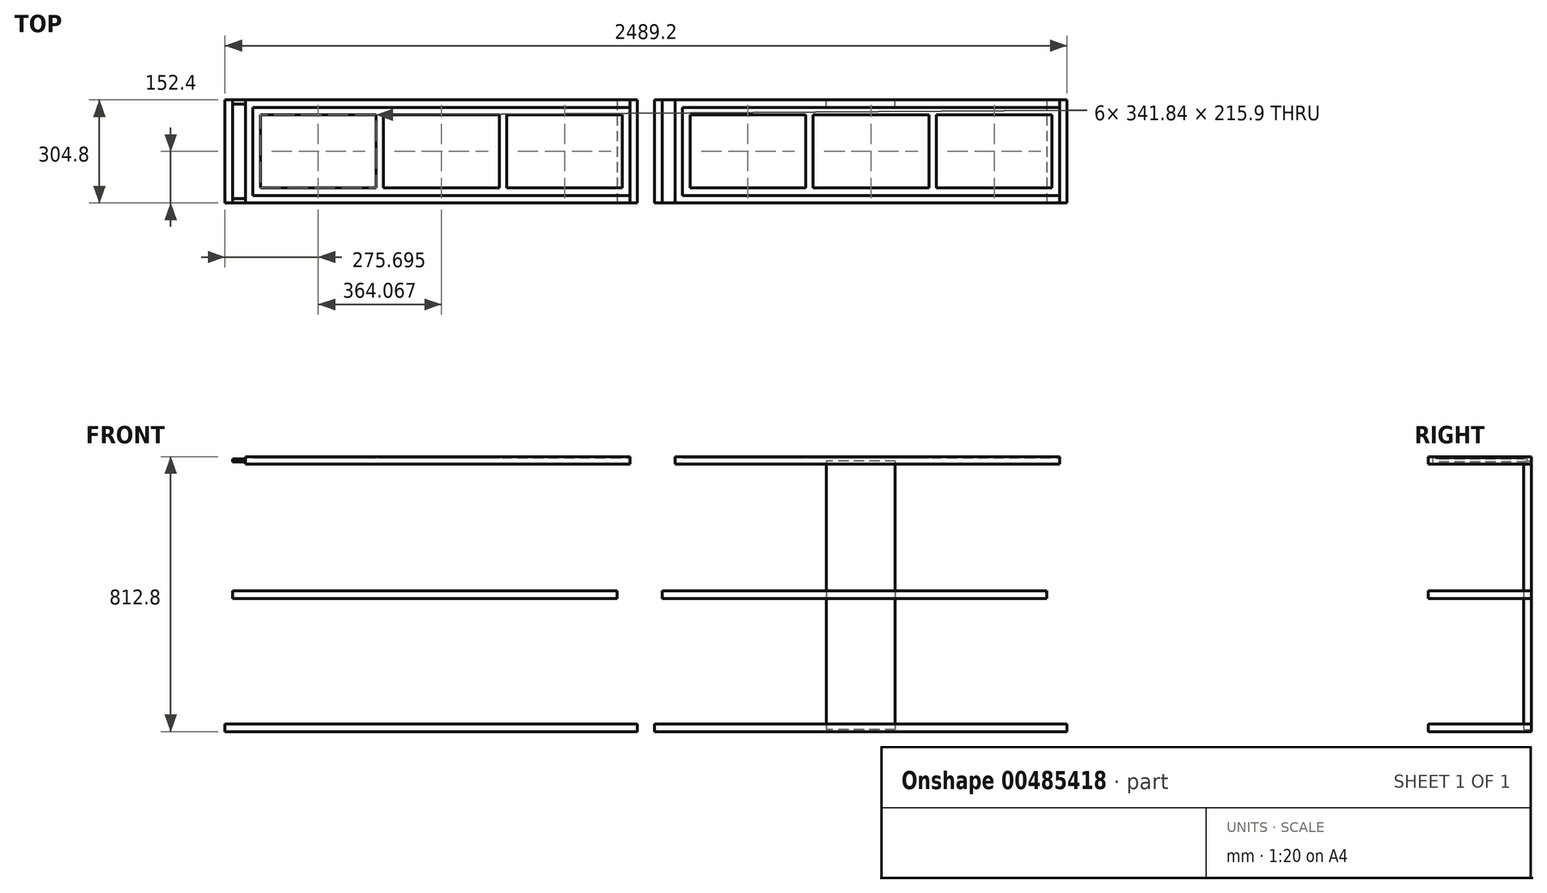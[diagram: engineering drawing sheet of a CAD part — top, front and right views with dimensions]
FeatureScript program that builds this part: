
annotation { "Feature Type Name" : "Feature", "Feature Type Description" : "" }
export const myFeature = defineFeature(function(context is Context, id is Id, definition is map)
    precondition{}
    {
        {
            var Q0;
            Q0=qCreatedBy(makeId("Front.planeOp"),FACE);
            var sketch = newSketch(context, id + "F0", { "sketchPlane" : qUnion([Q0])});
            skLineSegment(sketch, "E0.bottom", {"start": v(0, 22.22) * mm, "end": v(-1219.2, 22.22) * mm});
            skLineSegment(sketch, "E0.top", {"start": v(0, 0) * mm, "end": v(-1219.2, 0) * mm});
            skLineSegment(sketch, "E0.left", {"start": v(0, 22.22) * mm, "end": v(0, 0) * mm});
            skLineSegment(sketch, "E0.right", {"start": v(-1219.2, 22.22) * mm, "end": v(-1219.2, 0) * mm});
            skLineSegment(sketch, "E1.bottom", {"start": v(0, 22.22) * mm, "end": v(-22.23, 22.22) * mm});
            skLineSegment(sketch, "E1.top", {"start": v(0, 812.8) * mm, "end": v(-22.23, 812.8) * mm});
            skLineSegment(sketch, "E1.left", {"start": v(0, 22.22) * mm, "end": v(0, 812.8) * mm});
            skLineSegment(sketch, "E1.right", {"start": v(-22.23, 22.22) * mm, "end": v(-22.23, 812.8) * mm});
            skLineSegment(sketch, "E2.bottom", {"start": v(-1219.2, 22.22) * mm, "end": v(-1196.98, 22.22) * mm});
            skLineSegment(sketch, "E2.top", {"start": v(-1219.2, 812.8) * mm, "end": v(-1196.98, 812.8) * mm});
            skLineSegment(sketch, "E2.left", {"start": v(-1219.2, 22.22) * mm, "end": v(-1219.2, 812.8) * mm});
            skLineSegment(sketch, "E2.right", {"start": v(-1196.98, 22.22) * mm, "end": v(-1196.98, 812.8) * mm});
            skLineSegment(sketch, "E3.bottom", {"start": v(-1196.98, 393.7) * mm, "end": v(-60.33, 393.7) * mm});
            skLineSegment(sketch, "E3.top", {"start": v(-1196.98, 415.93) * mm, "end": v(-60.33, 415.93) * mm});
            skLineSegment(sketch, "E3.left", {"start": v(-1196.98, 393.7) * mm, "end": v(-1196.98, 415.93) * mm});
            skLineSegment(sketch, "E3.right", {"start": v(-60.33, 393.7) * mm, "end": v(-60.33, 415.93) * mm});
            skLineSegment(sketch, "E4.bottom", {"start": v(-22.23, 812.8) * mm, "end": v(-1158.88, 812.8) * mm});
            skLineSegment(sketch, "E4.top", {"start": v(-22.23, 790.58) * mm, "end": v(-1158.88, 790.57) * mm});
            skLineSegment(sketch, "E4.left", {"start": v(-22.23, 812.8) * mm, "end": v(-22.23, 790.58) * mm});
            skLineSegment(sketch, "E5.left", {"start": v(-1158.88, 812.8) * mm, "end": v(-1158.88, 790.57) * mm});
            skSolve(sketch);
        }
        {
            var Q0;
            {var subQ1=sQuery(id+"F0.wireOp",EDGE,"E2.bottom");Q0=makeQuery(id+"F0.imprint","IMPRINT",FACE,{"disambiguationData":[TD([[makeQuery(id+"F0.imprint","IMPRINT",EDGE,{"derivedFrom":subQ1}),1.0]])]});}
            var Q1;
            Q1=makeQuery(id+"F0.imprint","IMPRINT",FACE,{"disambiguationData":[TD([[makeQuery(id+"F0.imprint","IMPRINT",EDGE,{"derivedFrom":sQuery(id+"F0.wireOp",EDGE,"E3.bottom")}),1.0]])]});
            var Q2;
            Q2=makeQuery(id+"F0.imprint","IMPRINT",FACE,{"disambiguationData":[TD([[makeQuery(id+"F0.imprint","IMPRINT",EDGE,{"derivedFrom":sQuery(id+"F0.wireOp",EDGE,"E4.bottom")}),1.0]])]});
            var Q3;
            Q3=makeQuery(id+"F0.imprint","IMPRINT",FACE,{"disambiguationData":[TD([[makeQuery(id+"F0.imprint","IMPRINT",EDGE,{"derivedFrom":sQuery(id+"F0.wireOp",EDGE,"E1.bottom")}),-1.0]])]});
            var Q4;
            Q4=makeQuery(id+"F0.imprint","IMPRINT",FACE,{"disambiguationData":[TD([[makeQuery(id+"F0.imprint","IMPRINT",EDGE,{"derivedFrom":sQuery(id+"F0.wireOp",EDGE,"E0.bottom")}),1.0]])]});
            extrude(context, id + "F1", {"entities" : qUnion([Q0, Q1, Q2, Q3, Q4]), "oppositeDirection" : true, "depth" : 304.8 * mm});
        }
        {
            var Q0;
            Q0=makeQuery(id+"F1.opExtrude","SWEPT_FACE",FACE,{"disambiguationData":[OSD([sQuery(id+"F0.wireOp",EDGE,"E1.top"),sQuery(id+"F0.wireOp",EDGE,"E4.bottom")])]});
            var sketch = newSketch(context, id + "F2", { "sketchPlane" : qUnion([Q0])});
            skLineSegment(sketch, "E6.0", {"start": v(-1136.65, 22.23) * mm, "end": v(-22.23, 22.23) * mm});
            skLineSegment(sketch, "E6.1", {"start": v(-1136.65, 282.58) * mm, "end": v(-1136.65, 22.22) * mm});
            skLineSegment(sketch, "E6.2", {"start": v(-22.23, 282.58) * mm, "end": v(-1136.65, 282.58) * mm});
            skLineSegment(sketch, "E6.3", {"start": v(-22.23, 22.22) * mm, "end": v(-22.23, 282.58) * mm});
            skLineSegment(sketch, "E7.0", {"start": v(-44.45, 260.35) * mm, "end": v(-386.3, 260.35) * mm});
            skLineSegment(sketch, "E7.1", {"start": v(-44.45, 44.45) * mm, "end": v(-44.45, 260.35) * mm});
            skLineSegment(sketch, "E7.2", {"start": v(-1114.43, 44.45) * mm, "end": v(-772.58, 44.45) * mm});
            skLineSegment(sketch, "E7.3", {"start": v(-1114.43, 260.35) * mm, "end": v(-1114.43, 44.45) * mm});
            skLineSegment(sketch, "E8", {"start": v(-772.58, 260.35) * mm, "end": v(-772.58, 44.45) * mm});
            skLineSegment(sketch, "E9", {"start": v(-750.36, 260.35) * mm, "end": v(-750.36, 44.45) * mm});
            skLineSegment(sketch, "E10", {"start": v(-408.52, 260.35) * mm, "end": v(-408.52, 44.45) * mm});
            skLineSegment(sketch, "E11", {"start": v(-386.3, 260.35) * mm, "end": v(-386.3, 44.45) * mm});
            skLineSegment(sketch, "E12.trimOffspring", {"start": v(-772.58, 260.35) * mm, "end": v(-1114.43, 260.35) * mm});
            skLineSegment(sketch, "E13.trimOffspring", {"start": v(-750.36, 44.45) * mm, "end": v(-408.52, 44.45) * mm});
            skLineSegment(sketch, "E14.trimOffspring", {"start": v(-386.3, 44.45) * mm, "end": v(-44.45, 44.45) * mm});
            skLineSegment(sketch, "E15.trimOffspring", {"start": v(-408.52, 260.35) * mm, "end": v(-750.36, 260.35) * mm});
            skSolve(sketch);
        }
        {
            var Q0;
            Q0=makeQuery(id+"F2.imprint","IMPRINT",FACE,{"disambiguationData":[TD([[makeQuery(id+"F2.imprint","IMPRINT",EDGE,{"derivedFrom":sQuery(id+"F2.wireOp",EDGE,"E6.0")}),1.0]])]});
            extrude(context, id + "F3", {"entities" : qUnion([Q0]), "operationType" : NewBodyOperationType.REMOVE, "oppositeDirection" : true, "depth" : 3.17 * mm});
        }
        {
            var Q0;
            Q0=makeQuery(id+"F2.imprint","IMPRINT",FACE,{"disambiguationData":[TD([[makeQuery(id+"F2.imprint","IMPRINT",EDGE,{"derivedFrom":sQuery(id+"F2.wireOp",EDGE,"E6.0")}),1.0]])]});
            extrude(context, id + "F4", {"entities" : qUnion([Q0]), "oppositeDirection" : true, "depth" : 3.17 * mm});
        }
        {
            var Q0;
            Q0=makeQuery(id+"F1.opExtrude","SWEPT_BODY",BODY,{"disambiguationData":[OSD([sQuery(id+"F0.wireOp",EDGE,"E0.bottom"),sQuery(id+"F0.wireOp",EDGE,"E0.top"),sQuery(id+"F0.wireOp",EDGE,"E0.left"),sQuery(id+"F0.wireOp",EDGE,"E0.right"),sQuery(id+"F0.wireOp",EDGE,"E1.top"),sQuery(id+"F0.wireOp",EDGE,"E1.left"),sQuery(id+"F0.wireOp",EDGE,"E1.right"),sQuery(id+"F0.wireOp",EDGE,"E2.top"),sQuery(id+"F0.wireOp",EDGE,"E2.left"),sQuery(id+"F0.wireOp",EDGE,"E2.right"),sQuery(id+"F0.wireOp",EDGE,"E3.bottom"),sQuery(id+"F0.wireOp",EDGE,"E3.top"),sQuery(id+"F0.wireOp",EDGE,"E3.right"),sQuery(id+"F0.wireOp",EDGE,"E4.bottom"),sQuery(id+"F0.wireOp",EDGE,"E4.top"),sQuery(id+"F0.wireOp",EDGE,"E5.left")])]});
            transform(context, id + "F5", {"entities" : qUnion([Q0]), "transformType" : TransformType.TRANSLATION_3D, "dx" : 1270 * mm, "dy" : 0 * mm, "dz" : 0 * mm, "makeCopy" : true});
        }
        {
            var Q0;
            Q0=makeQuery(id+"F4.opExtrude","SWEPT_BODY",BODY,{"disambiguationData":[OSD([sQuery(id+"F2.wireOp",EDGE,"E6.0"),sQuery(id+"F2.wireOp",EDGE,"E6.1"),sQuery(id+"F2.wireOp",EDGE,"E6.2"),sQuery(id+"F2.wireOp",EDGE,"E6.3"),sQuery(id+"F2.wireOp",EDGE,"E7.0"),sQuery(id+"F2.wireOp",EDGE,"E7.1"),sQuery(id+"F2.wireOp",EDGE,"E7.2"),sQuery(id+"F2.wireOp",EDGE,"E7.3"),sQuery(id+"F2.wireOp",EDGE,"E8"),sQuery(id+"F2.wireOp",EDGE,"E9"),sQuery(id+"F2.wireOp",EDGE,"E10"),sQuery(id+"F2.wireOp",EDGE,"E11"),sQuery(id+"F2.wireOp",EDGE,"E12.trimOffspring"),sQuery(id+"F2.wireOp",EDGE,"E13.trimOffspring"),sQuery(id+"F2.wireOp",EDGE,"E14.trimOffspring"),sQuery(id+"F2.wireOp",EDGE,"E15.trimOffspring")])]});
            transform(context, id + "F6", {"entities" : qUnion([Q0]), "transformType" : TransformType.TRANSLATION_3D, "dx" : 1270 * mm, "dy" : 0 * mm, "dz" : 0 * mm, "makeCopy" : true});
        }
        {
            var Q0;
            Q0=makeQuery(id+"F5.opPattern","COPY",FACE,{"derivedFrom":makeQuery(id+"F1.opExtrude","CAP_FACE",FACE,{"disambiguationData":[OSD([sQuery(id+"F0.wireOp",EDGE,"E0.bottom"),sQuery(id+"F0.wireOp",EDGE,"E0.top"),sQuery(id+"F0.wireOp",EDGE,"E0.left"),sQuery(id+"F0.wireOp",EDGE,"E0.right"),sQuery(id+"F0.wireOp",EDGE,"E1.top"),sQuery(id+"F0.wireOp",EDGE,"E1.left"),sQuery(id+"F0.wireOp",EDGE,"E1.right"),sQuery(id+"F0.wireOp",EDGE,"E2.top"),sQuery(id+"F0.wireOp",EDGE,"E2.left"),sQuery(id+"F0.wireOp",EDGE,"E2.right"),sQuery(id+"F0.wireOp",EDGE,"E3.bottom"),sQuery(id+"F0.wireOp",EDGE,"E3.top"),sQuery(id+"F0.wireOp",EDGE,"E3.right"),sQuery(id+"F0.wireOp",EDGE,"E4.bottom"),sQuery(id+"F0.wireOp",EDGE,"E4.top"),sQuery(id+"F0.wireOp",EDGE,"E5.left")])],"isStart":false}),"instanceName":"1"});
            var sketch = newSketch(context, id + "F7", { "sketchPlane" : qUnion([Q0])});
            skLineSegment(sketch, "E16.bottom", {"start": v(-762, 800.1) * mm, "end": v(-558.8, 800.1) * mm});
            skLineSegment(sketch, "E16.top", {"start": v(-762, 6.35) * mm, "end": v(-558.8, 6.35) * mm});
            skLineSegment(sketch, "E16.left", {"start": v(-762, 800.1) * mm, "end": v(-762, 6.35) * mm});
            skLineSegment(sketch, "E16.right", {"start": v(-558.8, 800.1) * mm, "end": v(-558.8, 6.35) * mm});
            skSolve(sketch);
        }
        {
            var Q0;
            {var subQ0=sQuery(id+"F7.wireOp",EDGE,"E16.bottom");Q0=makeQuery(id+"F7.imprint","IMPRINT",FACE,{"disambiguationData":[TD([[makeQuery(id+"F7.imprint","IMPRINT",EDGE,{"derivedFrom":subQ0}),-1.0]])]});}
            var Q1;
            {var subQ0=sQuery(id+"F7.wireOp",EDGE,"E16.left");var subQ1=makeQuery(id+"F5.opPattern","COPY",EDGE,{"derivedFrom":makeQuery(id+"F1.opExtrude","CAP_EDGE",EDGE,{"disambiguationData":[OSD([sQuery(id+"F0.wireOp",EDGE,"E3.top")])],"isStart":false}),"instanceName":"1"});var subQ2=makeQuery(id+"F7.imprint","INTERSECT",VERTEX,{"derivedFrom":[subQ1,subQ0]});Q1=makeQuery(id+"F7.imprint","IMPRINT",FACE,{"disambiguationData":[TD([[makeQuery(id+"F7.imprint","IMPRINT",EDGE,{"disambiguationData":[TD([[subQ2,-1.0]])],"derivedFrom":subQ0}),1.0]])]});}
            var Q2;
            {var subQ0=sQuery(id+"F7.wireOp",EDGE,"E16.top");Q2=makeQuery(id+"F7.imprint","IMPRINT",FACE,{"disambiguationData":[TD([[makeQuery(id+"F7.imprint","IMPRINT",EDGE,{"derivedFrom":subQ0}),1.0]])]});}
            extrude(context, id + "F8", {"entities" : qUnion([Q0, Q1, Q2]), "operationType" : NewBodyOperationType.REMOVE, "oppositeDirection" : true, "depth" : 22.22 * mm});
        }
        {
            var Q0;
            {var subQ0=sQuery(id+"F7.wireOp",EDGE,"E16.left");var subQ1=makeQuery(id+"F5.opPattern","COPY",EDGE,{"derivedFrom":makeQuery(id+"F1.opExtrude","CAP_EDGE",EDGE,{"disambiguationData":[OSD([sQuery(id+"F0.wireOp",EDGE,"E4.top")])],"isStart":false}),"instanceName":"1"});var subQ2=makeQuery(id+"F7.imprint","INTERSECT",VERTEX,{"derivedFrom":[subQ1,subQ0]});Q0=makeQuery(id+"F7.imprint","IMPRINT",FACE,{"disambiguationData":[TD([[makeQuery(id+"F7.imprint","IMPRINT",EDGE,{"disambiguationData":[TD([[subQ2,-1.0]])],"derivedFrom":subQ0}),1.0]])]});}
            var Q1;
            {var subQ0=sQuery(id+"F7.wireOp",EDGE,"E16.bottom");Q1=makeQuery(id+"F7.imprint","IMPRINT",FACE,{"disambiguationData":[TD([[makeQuery(id+"F7.imprint","IMPRINT",EDGE,{"derivedFrom":subQ0}),-1.0]])]});}
            var Q2;
            {var subQ0=sQuery(id+"F7.wireOp",EDGE,"E16.left");var subQ1=makeQuery(id+"F5.opPattern","COPY",EDGE,{"derivedFrom":makeQuery(id+"F1.opExtrude","CAP_EDGE",EDGE,{"disambiguationData":[OSD([sQuery(id+"F0.wireOp",EDGE,"E3.top")])],"isStart":false}),"instanceName":"1"});var subQ2=makeQuery(id+"F7.imprint","INTERSECT",VERTEX,{"derivedFrom":[subQ1,subQ0]});Q2=makeQuery(id+"F7.imprint","IMPRINT",FACE,{"disambiguationData":[TD([[makeQuery(id+"F7.imprint","IMPRINT",EDGE,{"disambiguationData":[TD([[subQ2,-1.0]])],"derivedFrom":subQ0}),1.0]])]});}
            var Q3;
            {var subQ0=sQuery(id+"F7.wireOp",EDGE,"E16.left");var subQ1=makeQuery(id+"F5.opPattern","COPY",EDGE,{"derivedFrom":makeQuery(id+"F1.opExtrude","CAP_EDGE",EDGE,{"disambiguationData":[OSD([sQuery(id+"F0.wireOp",EDGE,"E3.bottom")])],"isStart":false}),"instanceName":"1"});var subQ2=makeQuery(id+"F7.imprint","INTERSECT",VERTEX,{"derivedFrom":[subQ1,subQ0]});Q3=makeQuery(id+"F7.imprint","IMPRINT",FACE,{"disambiguationData":[TD([[makeQuery(id+"F7.imprint","IMPRINT",EDGE,{"disambiguationData":[TD([[subQ2,-1.0]])],"derivedFrom":subQ0}),1.0]])]});}
            var Q4;
            {var subQ0=sQuery(id+"F7.wireOp",EDGE,"E16.top");Q4=makeQuery(id+"F7.imprint","IMPRINT",FACE,{"disambiguationData":[TD([[makeQuery(id+"F7.imprint","IMPRINT",EDGE,{"derivedFrom":subQ0}),1.0]])]});}
            extrude(context, id + "F9", {"entities" : qUnion([Q0, Q1, Q2, Q3, Q4]), "oppositeDirection" : true, "depth" : 22.22 * mm});
        }
        {
            var Q0;
            Q0=makeQuery(id+"F1.opExtrude","SWEPT_FACE",FACE,{"disambiguationData":[OSD([sQuery(id+"F0.wireOp",EDGE,"E5.left")])]});
            var sketch = newSketch(context, id + "F10", { "sketchPlane" : qUnion([Q0])});
            skLineSegment(sketch, "E17.bottom", {"start": v(-292.1, 806.45) * mm, "end": v(-12.7, 806.45) * mm});
            skLineSegment(sketch, "E17.top", {"start": v(-292.1, 796.93) * mm, "end": v(-12.7, 796.93) * mm});
            skLineSegment(sketch, "E17.left", {"start": v(-292.1, 806.45) * mm, "end": v(-292.1, 796.93) * mm});
            skLineSegment(sketch, "E17.right", {"start": v(-12.7, 806.45) * mm, "end": v(-12.7, 796.93) * mm});
            skSolve(sketch);
        }
        {
            var Q0;
            Q0=makeQuery(id+"F10.imprint","IMPRINT",FACE,{"disambiguationData":[TD([[makeQuery(id+"F10.imprint","IMPRINT",EDGE,{"derivedFrom":sQuery(id+"F10.wireOp",EDGE,"E17.bottom")}),-1.0]])]});
            extrude(context, id + "F11", {"entities" : qUnion([Q0]), "depth" : 38.1 * mm});
        }
    });
